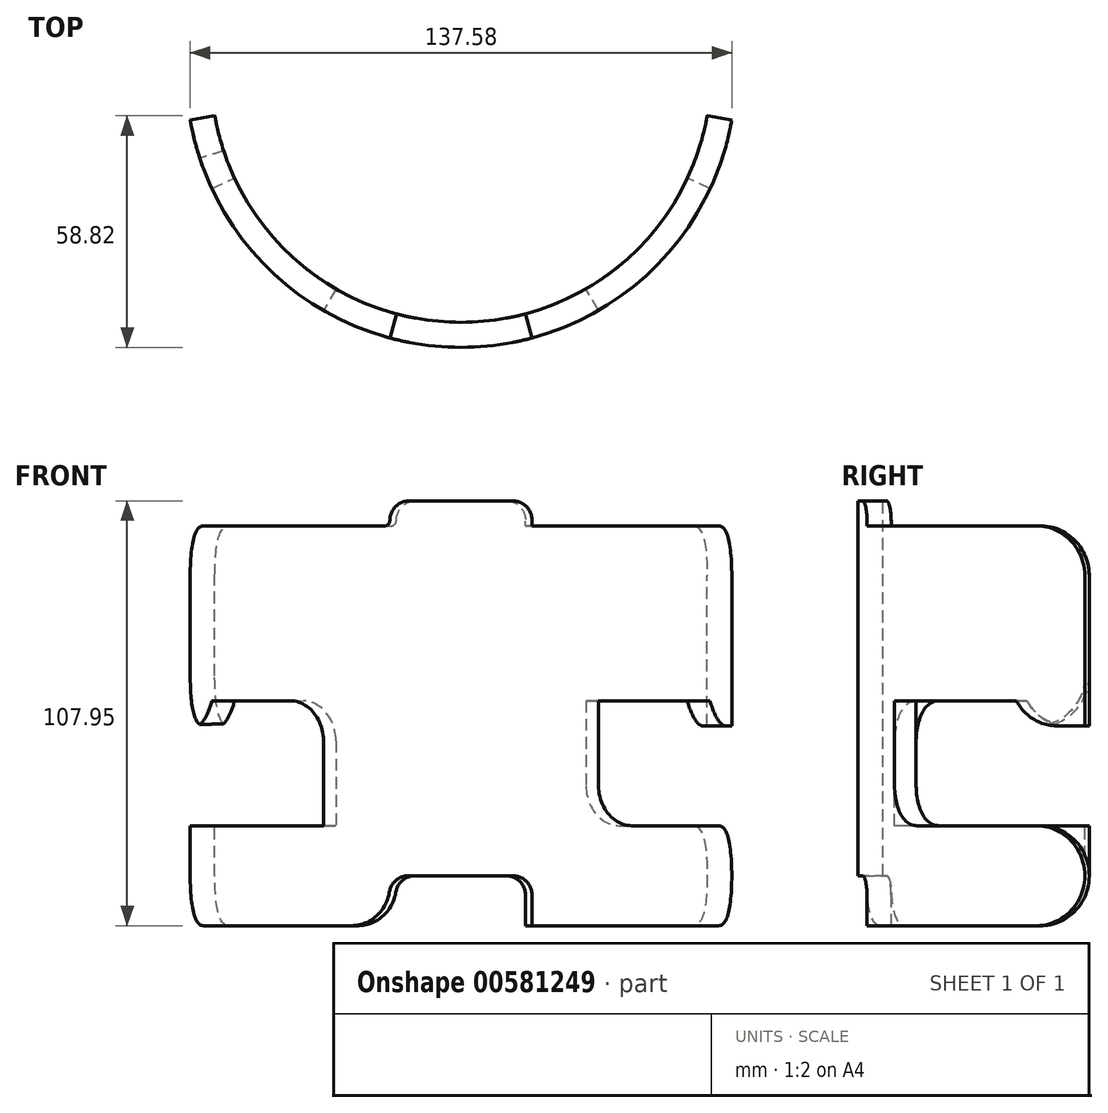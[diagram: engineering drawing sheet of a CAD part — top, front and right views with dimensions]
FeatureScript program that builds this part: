
annotation { "Feature Type Name" : "Feature", "Feature Type Description" : "" }
export const myFeature = defineFeature(function(context is Context, id is Id, definition is map)
    precondition{}
    {
        {
            var Q0;
            Q0=qCreatedBy(makeId("Right.planeOp"),FACE);
            var sketch = newSketch(context, id + "F0", { "sketchPlane" : qUnion([Q0])});
            skLineSegment(sketch, "E0", {"start": v(-69.85, 0) * mm, "end": v(-69.85, 63.5) * mm});
            skLineSegment(sketch, "E1", {"start": v(0, 76.2) * mm, "end": v(0, 0) * mm, "construction": true});
            skLineSegment(sketch, "E2", {"start": v(0, 0) * mm, "end": v(-63.5, 0) * mm, "construction": true});
            skLineSegment(sketch, "E3", {"start": v(-63.5, 0) * mm, "end": v(-63.5, 63.5) * mm});
            skLineSegment(sketch, "E4", {"start": v(-63.5, 0) * mm, "end": v(-63.5, 63.5) * mm, "construction": true});
            skLineSegment(sketch, "E5", {"start": v(-63.5, 63.5) * mm, "end": v(-69.85, 63.5) * mm});
            skLineSegment(sketch, "E6", {"start": v(-63.5, 0) * mm, "end": v(-63.5, -38.1) * mm});
            skLineSegment(sketch, "E7", {"start": v(-63.5, -38.1) * mm, "end": v(-69.85, -38.1) * mm});
            skLineSegment(sketch, "E8", {"start": v(-69.85, -38.1) * mm, "end": v(-69.85, 0) * mm});
            skSolve(sketch);
        }
        {
            var Q0;
            Q0 = qSketchRegion(id + "F0", true);
            var Q1;
            Q1=sQuery(id+"F0.wireOp",EDGE,"E1");
            revolve(context, id + "F1", {"entities" : qUnion([Q0]), "axis" : qUnion([Q1]), "revolveType" : RevolveType.SYMMETRIC, "angle" : 160 * degree});
        }
        {
            var Q0;
            Q0=qCreatedBy(makeId("Right.planeOp"),FACE);
            var sketch = newSketch(context, id + "F2", { "sketchPlane" : qUnion([Q0])});
            skLineSegment(sketch, "E9", {"start": v(0, 0) * mm, "end": v(-63.5, 0) * mm, "construction": true});
            skLineSegment(sketch, "E10", {"start": v(-69.85, 0) * mm, "end": v(-69.85, 12.7) * mm});
            skLineSegment(sketch, "E11", {"start": v(-69.85, 12.7) * mm, "end": v(-63.5, 12.7) * mm});
            skLineSegment(sketch, "E12", {"start": v(-63.5, 12.7) * mm, "end": v(-63.5, 0) * mm});
            skLineSegment(sketch, "E13", {"start": v(-63.5, 0) * mm, "end": v(-69.85, 0) * mm});
            skLineSegment(sketch, "E14", {"start": v(0, 0) * mm, "end": v(0, 25.4) * mm, "construction": true});
            skLineSegment(sketch, "E15", {"start": v(-63.5, 0) * mm, "end": v(-63.5, -12.7) * mm});
            skLineSegment(sketch, "E16", {"start": v(-63.5, -12.7) * mm, "end": v(-69.85, -12.7) * mm});
            skLineSegment(sketch, "E17", {"start": v(-69.85, -12.7) * mm, "end": v(-69.85, 0) * mm});
            skSolve(sketch);
        }
        {
            var Q0;
            Q0 = qSketchRegion(id + "F2", true);
            var Q1;
            Q1=sQuery(id+"F2.wireOp",EDGE,"E14");
            revolve(context, id + "F3", {"operationType" : NewBodyOperationType.REMOVE, "entities" : qUnion([Q0]), "axis" : qUnion([Q1]), "revolveType" : RevolveType.SYMMETRIC, "oppositeDirection" : true, "angle" : 160 * degree});
        }
        {
            var Q0;
            Q0=qCreatedBy(makeId("Right.planeOp"),FACE);
            var sketch = newSketch(context, id + "F4", { "sketchPlane" : qUnion([Q0])});
            skLineSegment(sketch, "E18", {"start": v(0, 0) * mm, "end": v(-69.85, 0) * mm, "construction": true});
            skLineSegment(sketch, "E19", {"start": v(-69.85, 0) * mm, "end": v(-69.85, 63.5) * mm, "construction": true});
            skLineSegment(sketch, "E20", {"start": v(-69.85, 63.5) * mm, "end": v(-63.5, 63.5) * mm});
            skLineSegment(sketch, "E21", {"start": v(-63.5, 63.5) * mm, "end": v(-63.5, 69.85) * mm});
            skLineSegment(sketch, "E22", {"start": v(-63.5, 69.85) * mm, "end": v(-69.85, 69.85) * mm});
            skLineSegment(sketch, "E23", {"start": v(-69.85, 69.85) * mm, "end": v(-69.85, 63.5) * mm});
            skLineSegment(sketch, "E24", {"start": v(0, 0) * mm, "end": v(0, 76.2) * mm, "construction": true});
            skSolve(sketch);
        }
        {
            var Q0;
            Q0 = qSketchRegion(id + "F4", true);
            var Q1;
            Q1=sQuery(id+"F4.wireOp",EDGE,"E24");
            revolve(context, id + "F5", {"operationType" : NewBodyOperationType.ADD, "entities" : qUnion([Q0]), "axis" : qUnion([Q1]), "revolveType" : RevolveType.SYMMETRIC, "angle" : 30 * degree});
        }
        {
            var Q0;
            Q0=qCreatedBy(makeId("Right.planeOp"),FACE);
            var sketch = newSketch(context, id + "F6", { "sketchPlane" : qUnion([Q0])});
            skLineSegment(sketch, "E25", {"start": v(0, 0) * mm, "end": v(-69.85, 0) * mm, "construction": true});
            skLineSegment(sketch, "E26", {"start": v(-69.85, 0) * mm, "end": v(-69.85, -25.4) * mm, "construction": true});
            skLineSegment(sketch, "E27", {"start": v(-69.85, -25.4) * mm, "end": v(-69.85, -38.1) * mm});
            skLineSegment(sketch, "E28", {"start": v(-69.85, -38.1) * mm, "end": v(-63.5, -38.1) * mm});
            skLineSegment(sketch, "E29", {"start": v(-63.5, -38.1) * mm, "end": v(-63.5, -25.4) * mm});
            skLineSegment(sketch, "E30", {"start": v(-63.5, -25.4) * mm, "end": v(-69.85, -25.4) * mm});
            skLineSegment(sketch, "E31", {"start": v(0, 0) * mm, "end": v(0, -25.4) * mm, "construction": true});
            skSolve(sketch);
        }
        {
            var Q0;
            Q0 = qSketchRegion(id + "F6", true);
            var Q1;
            Q1=sQuery(id+"F6.wireOp",EDGE,"E31");
            revolve(context, id + "F7", {"operationType" : NewBodyOperationType.REMOVE, "entities" : qUnion([Q0]), "axis" : qUnion([Q1]), "revolveType" : RevolveType.SYMMETRIC, "oppositeDirection" : true, "angle" : 30 * degree});
        }
        {
            var Q0;
            Q0=qCreatedBy(makeId("Right.planeOp"),FACE);
            var sketch = newSketch(context, id + "F8", { "sketchPlane" : qUnion([Q0])});
            skLineSegment(sketch, "E32", {"start": v(0, 0) * mm, "end": v(-69.85, 0) * mm, "construction": true});
            skLineSegment(sketch, "E33", {"start": v(-69.85, 0) * mm, "end": v(-69.85, 19.05) * mm});
            skLineSegment(sketch, "E34", {"start": v(-69.85, 19.05) * mm, "end": v(-63.5, 19.05) * mm});
            skLineSegment(sketch, "E35", {"start": v(-63.5, 19.05) * mm, "end": v(-63.5, 0) * mm});
            skLineSegment(sketch, "E36", {"start": v(-63.5, 0) * mm, "end": v(-69.85, 0) * mm});
            skLineSegment(sketch, "E37", {"start": v(0, 0) * mm, "end": v(0, 27.36) * mm, "construction": true});
            skSolve(sketch);
        }
        {
            var Q0;
            Q0 = qSketchRegion(id + "F8", true);
            var Q1;
            Q1=sQuery(id+"F8.wireOp",EDGE,"E37");
            revolve(context, id + "F9", {"operationType" : NewBodyOperationType.REMOVE, "entities" : qUnion([Q0]), "axis" : qUnion([Q1]), "revolveType" : RevolveType.SYMMETRIC, "oppositeDirection" : true, "angle" : 130 * degree});
        }
        {
            var Q0;
            Q0=qCreatedBy(makeId("Right.planeOp"),FACE);
            var sketch = newSketch(context, id + "F10", { "sketchPlane" : qUnion([Q0])});
            skLineSegment(sketch, "E38", {"start": v(0, 0) * mm, "end": v(-69.85, 0) * mm, "construction": true});
            skLineSegment(sketch, "E39", {"start": v(-69.85, 0) * mm, "end": v(-69.85, -12.7) * mm});
            skLineSegment(sketch, "E40", {"start": v(-69.85, 0) * mm, "end": v(-69.85, 19.05) * mm});
            skLineSegment(sketch, "E41", {"start": v(-69.85, 19.05) * mm, "end": v(-63.5, 19.05) * mm});
            skLineSegment(sketch, "E42", {"start": v(-63.5, 19.05) * mm, "end": v(-63.5, -12.7) * mm});
            skLineSegment(sketch, "E43", {"start": v(-63.5, -12.7) * mm, "end": v(-69.85, -12.7) * mm});
            skLineSegment(sketch, "E44", {"start": v(0, 0) * mm, "end": v(0, 34.25) * mm, "construction": true});
            skSolve(sketch);
        }
        {
            var Q0;
            Q0 = qSketchRegion(id + "F10", true);
            var Q1;
            Q1=sQuery(id+"F10.wireOp",EDGE,"E44");
            revolve(context, id + "F11", {"operationType" : NewBodyOperationType.ADD, "entities" : qUnion([Q0]), "axis" : qUnion([Q1]), "revolveType" : RevolveType.SYMMETRIC, "angle" : 60 * degree});
        }
        {
            var Q0;
            Q0=makeQuery(id+"F1.opRevolve","CAP_EDGE",EDGE,{"disambiguationData":[OSD([sQuery(id+"F0.wireOp",EDGE,"E5")])],"isStart":false});
            var Q1;
            Q1=makeQuery(id+"F1.opRevolve","CAP_EDGE",EDGE,{"disambiguationData":[OSD([sQuery(id+"F0.wireOp",EDGE,"oOZxLurU-VgsW-r99A-rwFG-M9Z4akLb4hXM")])],"isStart":false});
            var Q2;
            Q2=makeQuery(id+"F1.opRevolve","CAP_EDGE",EDGE,{"disambiguationData":[OSD([sQuery(id+"F0.wireOp",EDGE,"E5")])],"isStart":true});
            var Q3;
            Q3=makeQuery(id+"F1.opRevolve","CAP_EDGE",EDGE,{"disambiguationData":[OSD([sQuery(id+"F0.wireOp",EDGE,"oOZxLurU-VgsW-r99A-rwFG-M9Z4akLb4hXM")])],"isStart":true});
            var Q4;
            Q4=makeQuery(id+"F3.boolean.opBoolean","COPY",EDGE,{"derivedFrom":makeQuery(id+"F3.opRevolve","CAP_EDGE",EDGE,{"disambiguationData":[OSD([sQuery(id+"F2.wireOp",EDGE,"E11")])],"isStart":false})});
            var Q5;
            Q5=makeQuery(id+"F9.boolean.opBoolean","INTERSECT",EDGE,{"derivedFrom":[makeQuery(id+"F3.boolean.opBoolean","COPY",FACE,{"derivedFrom":makeQuery(id+"F3.opRevolve","SWEPT_FACE",FACE,{"disambiguationData":[OSD([sQuery(id+"F2.wireOp",EDGE,"E11")])]})}),makeQuery(id+"F9.opRevolve","CAP_FACE",FACE,{"disambiguationData":[OSD([sQuery(id+"F8.wireOp",EDGE,"E33"),sQuery(id+"F8.wireOp",EDGE,"E34"),sQuery(id+"F8.wireOp",EDGE,"E35"),sQuery(id+"F8.wireOp",EDGE,"E36")])],"isStart":false})]});
            var Q6;
            Q6=makeQuery(id+"F9.boolean.opBoolean","INTERSECT",EDGE,{"derivedFrom":[makeQuery(id+"F3.boolean.opBoolean","COPY",FACE,{"derivedFrom":makeQuery(id+"F3.opRevolve","SWEPT_FACE",FACE,{"disambiguationData":[OSD([sQuery(id+"F2.wireOp",EDGE,"E11")])]})}),makeQuery(id+"F9.opRevolve","CAP_FACE",FACE,{"disambiguationData":[OSD([sQuery(id+"F8.wireOp",EDGE,"E33"),sQuery(id+"F8.wireOp",EDGE,"E34"),sQuery(id+"F8.wireOp",EDGE,"E35"),sQuery(id+"F8.wireOp",EDGE,"E36")])],"isStart":true})]});
            var Q7;
            Q7=makeQuery(id+"F3.boolean.opBoolean","COPY",EDGE,{"derivedFrom":makeQuery(id+"F3.opRevolve","CAP_EDGE",EDGE,{"disambiguationData":[OSD([sQuery(id+"F2.wireOp",EDGE,"E11")])],"isStart":true})});
            var Q8;
            Q8=makeQuery(id+"F3.boolean.opBoolean","COPY",EDGE,{"derivedFrom":makeQuery(id+"F3.opRevolve","CAP_EDGE",EDGE,{"disambiguationData":[OSD([sQuery(id+"F2.wireOp",EDGE,"E16")])],"isStart":true})});
            var Q9;
            Q9=makeQuery(id+"F1.opRevolve","CAP_EDGE",EDGE,{"disambiguationData":[OSD([sQuery(id+"F0.wireOp",EDGE,"E7")])],"isStart":true});
            var Q10;
            Q10=makeQuery(id+"F1.opRevolve","CAP_EDGE",EDGE,{"disambiguationData":[OSD([sQuery(id+"F0.wireOp",EDGE,"E7")])],"isStart":false});
            var Q11;
            Q11=makeQuery(id+"F3.boolean.opBoolean","COPY",EDGE,{"derivedFrom":makeQuery(id+"F3.opRevolve","CAP_EDGE",EDGE,{"disambiguationData":[OSD([sQuery(id+"F2.wireOp",EDGE,"E16")])],"isStart":false})});
            fillet(context, id + "F12", {"entities" : qUnion([Q0, Q1, Q2, Q3, Q4, Q5, Q6, Q7, Q8, Q9, Q10, Q11]), "radius" : 12.7 * mm, "tangentPropagation" : true, "allowEdgeOverflow" : false});
        }
        {
            var Q0;
            Q0=makeQuery(id+"F11.opRevolve","CAP_EDGE",EDGE,{"disambiguationData":[OSD([sQuery(id+"F10.wireOp",EDGE,"E41")])],"isStart":false});
            var Q1;
            Q1=makeQuery(id+"F11.opRevolve","CAP_EDGE",EDGE,{"disambiguationData":[OSD([sQuery(id+"F10.wireOp",EDGE,"E43")])],"isStart":false});
            var Q2;
            Q2=makeQuery(id+"F11.opRevolve","CAP_EDGE",EDGE,{"disambiguationData":[OSD([sQuery(id+"F10.wireOp",EDGE,"E41")])],"isStart":true});
            var Q3;
            Q3=makeQuery(id+"F11.opRevolve","CAP_EDGE",EDGE,{"disambiguationData":[OSD([sQuery(id+"F10.wireOp",EDGE,"E43")])],"isStart":true});
            var Q4;
            Q4=makeQuery(id+"F7.boolean.opBoolean","COPY",EDGE,{"derivedFrom":makeQuery(id+"F7.opRevolve","CAP_EDGE",EDGE,{"disambiguationData":[OSD([sQuery(id+"F6.wireOp",EDGE,"E28")])],"isStart":false})});
            var Q5;
            Q5=makeQuery(id+"F7.boolean.opBoolean","COPY",EDGE,{"derivedFrom":makeQuery(id+"F7.opRevolve","CAP_EDGE",EDGE,{"disambiguationData":[OSD([sQuery(id+"F6.wireOp",EDGE,"E28")])],"isStart":true})});
            fillet(context, id + "F13", {"entities" : qUnion([Q0, Q1, Q2, Q3, Q4, Q5]), "radius" : 10.16 * mm, "tangentPropagation" : true, "allowEdgeOverflow" : false});
        }
        {
            var Q0;
            Q0=makeQuery(id+"F5.opRevolve","CAP_EDGE",EDGE,{"disambiguationData":[OSD([sQuery(id+"F4.wireOp",EDGE,"E20")])],"isStart":true});
            var Q1;
            Q1=makeQuery(id+"F5.opRevolve","CAP_EDGE",EDGE,{"disambiguationData":[OSD([sQuery(id+"F4.wireOp",EDGE,"E20")])],"isStart":false});
            fillet(context, id + "F14", {"entities" : qUnion([Q0, Q1]), "radius" : 1.27 * mm, "tangentPropagation" : true, "allowEdgeOverflow" : false});
        }
        {
            var Q0;
            Q0=makeQuery(id+"F5.opRevolve","CAP_EDGE",EDGE,{"disambiguationData":[OSD([sQuery(id+"F4.wireOp",EDGE,"E22")])],"isStart":false});
            var Q1;
            Q1=makeQuery(id+"F5.opRevolve","CAP_EDGE",EDGE,{"disambiguationData":[OSD([sQuery(id+"F4.wireOp",EDGE,"E22")])],"isStart":true});
            var Q2;
            Q2=makeQuery(id+"F7.boolean.opBoolean","COPY",EDGE,{"derivedFrom":makeQuery(id+"F7.opRevolve","CAP_EDGE",EDGE,{"disambiguationData":[OSD([sQuery(id+"F6.wireOp",EDGE,"E30")])],"isStart":true})});
            var Q3;
            Q3=makeQuery(id+"F7.boolean.opBoolean","COPY",EDGE,{"derivedFrom":makeQuery(id+"F7.opRevolve","CAP_EDGE",EDGE,{"disambiguationData":[OSD([sQuery(id+"F6.wireOp",EDGE,"E30")])],"isStart":false})});
            fillet(context, id + "F15", {"entities" : qUnion([Q0, Q1, Q2, Q3]), "radius" : 5.08 * mm, "tangentPropagation" : true, "allowEdgeOverflow" : false});
        }
    });
